# Revit family: ASL_64_Series_al_door_100mm_jamb_1
name_source: partatom
category: Detail Items
revit_build: Autodesk Revit 2018 (Build: 20170223_1515(x64)
units: mm (PartAtom-declared; Revit-internal decimal feet)

## family parameters
Rotate with component = No
Section Shape = Not Defined
Shared = Yes

## types (7) — shared parameters
Manufacturer = Aluminate Solutions Limited

## per-type parameters (varying)
| type | ASL Door Suite 100mm | ASL Door Suite 100mm Option | Door Depth | Door Stop_50 | Flush Infill | Glazing | Headsection_ASL_405 | Headsection_ASL_546 | Hinge_Single | Raven Seal | Technical Info | Type Comments |
| Double Action ASL Hinge Stile Door Suite 100mm | Yes | ASL_Door Suite_Stile_100mm : Hinge Stile Hinge Door 100mm | 22 mm  [stored 0.0721785 ft] | No | Yes | No | No | Yes | No | No | http://www.productspec.net | ASL 64 Series Jamb 1 With Double Action ASL 100mm Hinge Stile Door Suite |
| Single Action ASL Hinge Stile Door Suite 100mm | Yes | ASL_Door Suite_Stile_100mm : Hinge Stile Hinge Door 100mm | 46 mm  [stored 0.150919 ft] | Yes | No | No | No | Yes | Yes | No | www.aluminate.nz | ASL 64 Series Jamb 1 With Single Action ASL 100mm Hinge Stile Door Suite |
| Single Action ASL Lockset Stile Door Suite 100mm | Yes | ASL_Door Suite_Stile_100mm : Lockset Stile Hinge Door 100mm | 52 mm | No | No | No | Yes | No | No | Yes | www.aluminate.nz | ASL 64 Jamb 1 With Single Action ASL 100mm Lockset Stile Door Suite |
| Glazing | No | ASL_Door Suite_Stile_100mm : Hinge Stile Hinge Door 100mm | 51 mm | No | No | Yes | No | Yes | No | No | www.aluminate.nz | ASL 64 Series Jamb 1 With Glazing |
| Double Action ASL Lockset Stile Door Suite 100mm | Yes | ASL_Door Suite_Stile_100mm : Lockset Stile Double Action Hinge, Pviot and Sliding Door 100mm | 22 mm  [stored 0.0721785 ft] | No | Yes | No | No | Yes | No | No | www.aluminate.nz | ASL 64 Series Jamb 1 With Double Action ASL 100mm Lockset Stile Door Suite |
| Single Action Raven Seal ASL Hinge Stile Door Suite 100mm | Yes | ASL_Door Suite_Stile_100mm : Hinge Stile Hinge Door 100mm | 52 mm | No | No | No | Yes | No | Yes | Yes | www.aluminate.nz | ASL 64 Series Jamb 1 With Single Action Raven Seal ASL 100mm Hinge Stile Door Suite |
| Single Action Raven Seal ASL Suite Lockset Stile Door Suite 100mm | Yes | ASL_Door Suite_Stile_100mm : Lockset Stile Hinge Door 100mm | 52 mm | No | No | No | Yes | No | No | Yes | www.aluminate.nz | ASL 64 Series 64 Jamb 1 With Single Action Raven Seal ASL 100mm Suite Lockset Stile Door Suite |

note: [stored X ft] marks values corroborated as IEEE doubles in the binary element streams (Revit-internal decimal feet)

## geometry (parser evidence)
native form markers: Sweep x15
no freeform markers — native parametric forms only
